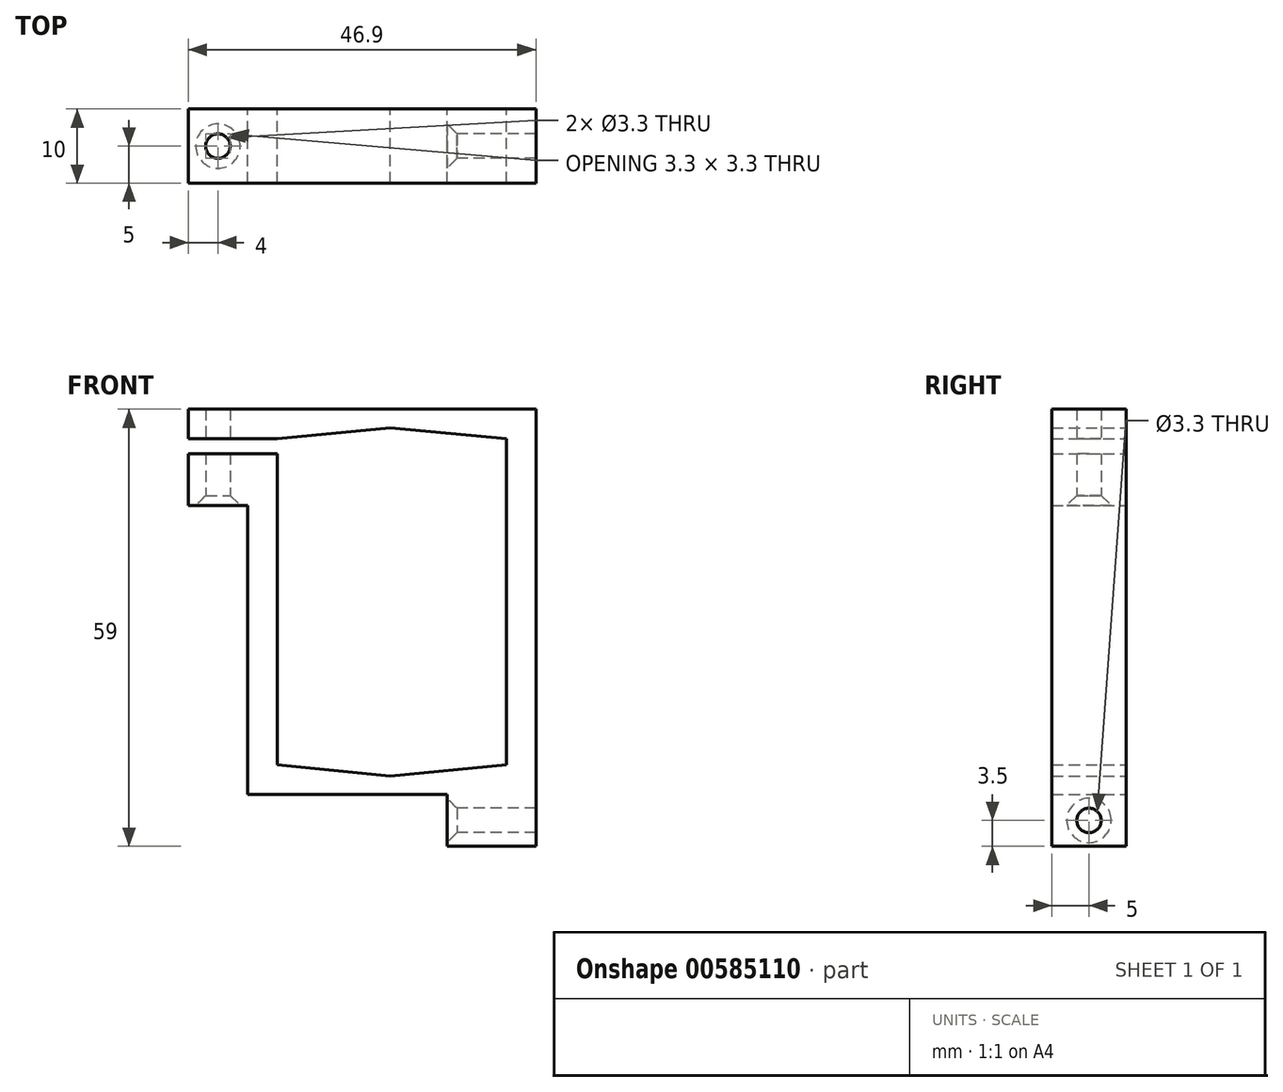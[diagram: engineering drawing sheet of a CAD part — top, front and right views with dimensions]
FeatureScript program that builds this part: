
annotation { "Feature Type Name" : "Feature", "Feature Type Description" : "" }
export const myFeature = defineFeature(function(context is Context, id is Id, definition is map)
    precondition{}
    {
        {
            var Q0;
            Q0=qCreatedBy(makeId("Front.planeOp"),FACE);
            var sketch = newSketch(context, id + "F0", { "sketchPlane" : qUnion([Q0])});
            skLineSegment(sketch, "E0", {"start": v(0, 0) * mm, "end": v(0, 44) * mm});
            skLineSegment(sketch, "E1", {"start": v(-30.9, 44) * mm, "end": v(-42.9, 44) * mm});
            skLineSegment(sketch, "E2", {"start": v(-42.9, 44) * mm, "end": v(-42.9, 48) * mm});
            skLineSegment(sketch, "E3", {"start": v(-42.9, 48) * mm, "end": v(4, 48) * mm});
            skLineSegment(sketch, "E4", {"start": v(4, 48) * mm, "end": v(4, -11) * mm});
            skLineSegment(sketch, "E5", {"start": v(4, -11) * mm, "end": v(-8, -11) * mm});
            skLineSegment(sketch, "E6", {"start": v(-34.9, -4) * mm, "end": v(-34.9, 35) * mm});
            skLineSegment(sketch, "E7", {"start": v(-34.9, 35) * mm, "end": v(-42.9, 35) * mm});
            skLineSegment(sketch, "E8", {"start": v(-42.9, 35) * mm, "end": v(-42.9, 42) * mm});
            skLineSegment(sketch, "E9", {"start": v(-42.9, 42) * mm, "end": v(-30.9, 42) * mm});
            skLineSegment(sketch, "E10", {"start": v(-30.9, 42) * mm, "end": v(-30.9, 0) * mm});
            skLineSegment(sketch, "E11", {"start": v(-34.9, -4) * mm, "end": v(-8, -4) * mm});
            skLineSegment(sketch, "E12", {"start": v(-8, -4) * mm, "end": v(-8, -11) * mm});
            skLineSegment(sketch, "E13", {"start": v(-30.9, 44) * mm, "end": v(-15.65, 45.5) * mm});
            skLineSegment(sketch, "E14", {"start": v(-15.65, 45.5) * mm, "end": v(0, 44) * mm});
            skLineSegment(sketch, "E15", {"start": v(-30.9, 0) * mm, "end": v(-15.65, -1.5) * mm});
            skLineSegment(sketch, "E16", {"start": v(-15.65, -1.5) * mm, "end": v(0, 0) * mm});
            skSolve(sketch);
        }
        {
            var Q0;
            Q0 = qSketchRegion(id + "F0", true);
            extrude(context, id + "F1", {"entities" : qUnion([Q0]), "depth" : 10 * mm, "offsetDistance" : 25 * mm});
        }
        {
            var Q0;
            Q0=makeQuery(id+"F1.opExtrude","SWEPT_FACE",FACE,{"disambiguationData":[OSD([sQuery(id+"F0.wireOp",EDGE,"E7")])]});
            var sketch = newSketch(context, id + "F2", { "sketchPlane" : qUnion([Q0])});
            skPoint(sketch, "E17", {"position": v(-38.9, 5) * mm});
            skLineSegment(sketch, "E18", {"start": v(-34.9, 10) * mm, "end": v(-42.9, 0) * mm, "construction": true});
            skSolve(sketch);
        }
        {
            var Q0;
            Q0=sQuery(id+"F2.wireOp",VERTEX,"E17");
            var Q1;
            Q1=makeQuery(id+"F1.opExtrude","SWEPT_BODY",BODY,{"disambiguationData":[OSD([sQuery(id+"F0.wireOp",EDGE,"E0"),sQuery(id+"F0.wireOp",EDGE,"E1"),sQuery(id+"F0.wireOp",EDGE,"E2"),sQuery(id+"F0.wireOp",EDGE,"E3"),sQuery(id+"F0.wireOp",EDGE,"E4"),sQuery(id+"F0.wireOp",EDGE,"E5"),sQuery(id+"F0.wireOp",EDGE,"E6"),sQuery(id+"F0.wireOp",EDGE,"E7"),sQuery(id+"F0.wireOp",EDGE,"E8"),sQuery(id+"F0.wireOp",EDGE,"E9"),sQuery(id+"F0.wireOp",EDGE,"E10"),sQuery(id+"F0.wireOp",EDGE,"igm1QySI-kFEP-fKqk-pehW-aXRtRxKip1QK"),sQuery(id+"F0.wireOp",EDGE,"E11"),sQuery(id+"F0.wireOp",EDGE,"E12")])]});
            hole(context, id + "F3", {"style" : HoleStyle.C_SINK, "endStyle" : HoleEndStyle.THROUGH, "holeDiameter" : 3.3 * mm, "cSinkDiameter" : 6 * mm, "cSinkAngle" : 90 * degree, "majorDiameter" : 5 * mm, "isTappedThrough" : true, "tappedDepth" : 12 * mm, "tapClearance" : 3, "locations" : qUnion([Q0]), "scope" : qUnion([Q1])});
        }
        {
            var Q0;
            Q0=makeQuery(id+"F1.opExtrude","SWEPT_FACE",FACE,{"disambiguationData":[OSD([sQuery(id+"F0.wireOp",EDGE,"E12")])]});
            var sketch = newSketch(context, id + "F4", { "sketchPlane" : qUnion([Q0])});
            skLineSegment(sketch, "E19", {"start": v(0, -4) * mm, "end": v(10, -11) * mm, "construction": true});
            skPoint(sketch, "E20", {"position": v(5, -7.5) * mm});
            skSolve(sketch);
        }
        {
            var Q0;
            Q0=sQuery(id+"F4.wireOp",VERTEX,"E20");
            var Q1;
            Q1=makeQuery(id+"F1.opExtrude","SWEPT_BODY",BODY,{"disambiguationData":[OSD([sQuery(id+"F0.wireOp",EDGE,"E0"),sQuery(id+"F0.wireOp",EDGE,"E1"),sQuery(id+"F0.wireOp",EDGE,"E2"),sQuery(id+"F0.wireOp",EDGE,"E3"),sQuery(id+"F0.wireOp",EDGE,"E4"),sQuery(id+"F0.wireOp",EDGE,"E5"),sQuery(id+"F0.wireOp",EDGE,"E6"),sQuery(id+"F0.wireOp",EDGE,"E7"),sQuery(id+"F0.wireOp",EDGE,"E8"),sQuery(id+"F0.wireOp",EDGE,"E9"),sQuery(id+"F0.wireOp",EDGE,"E10"),sQuery(id+"F0.wireOp",EDGE,"igm1QySI-kFEP-fKqk-pehW-aXRtRxKip1QK"),sQuery(id+"F0.wireOp",EDGE,"E11"),sQuery(id+"F0.wireOp",EDGE,"E12")])]});
            hole(context, id + "F5", {"style" : HoleStyle.C_SINK, "endStyle" : HoleEndStyle.THROUGH, "holeDiameter" : 3.3 * mm, "cSinkDiameter" : 6 * mm, "cSinkAngle" : 90 * degree, "majorDiameter" : 5 * mm, "isTappedThrough" : true, "tappedDepth" : 12 * mm, "tapClearance" : 3, "locations" : qUnion([Q0]), "scope" : qUnion([Q1])});
        }
    });
